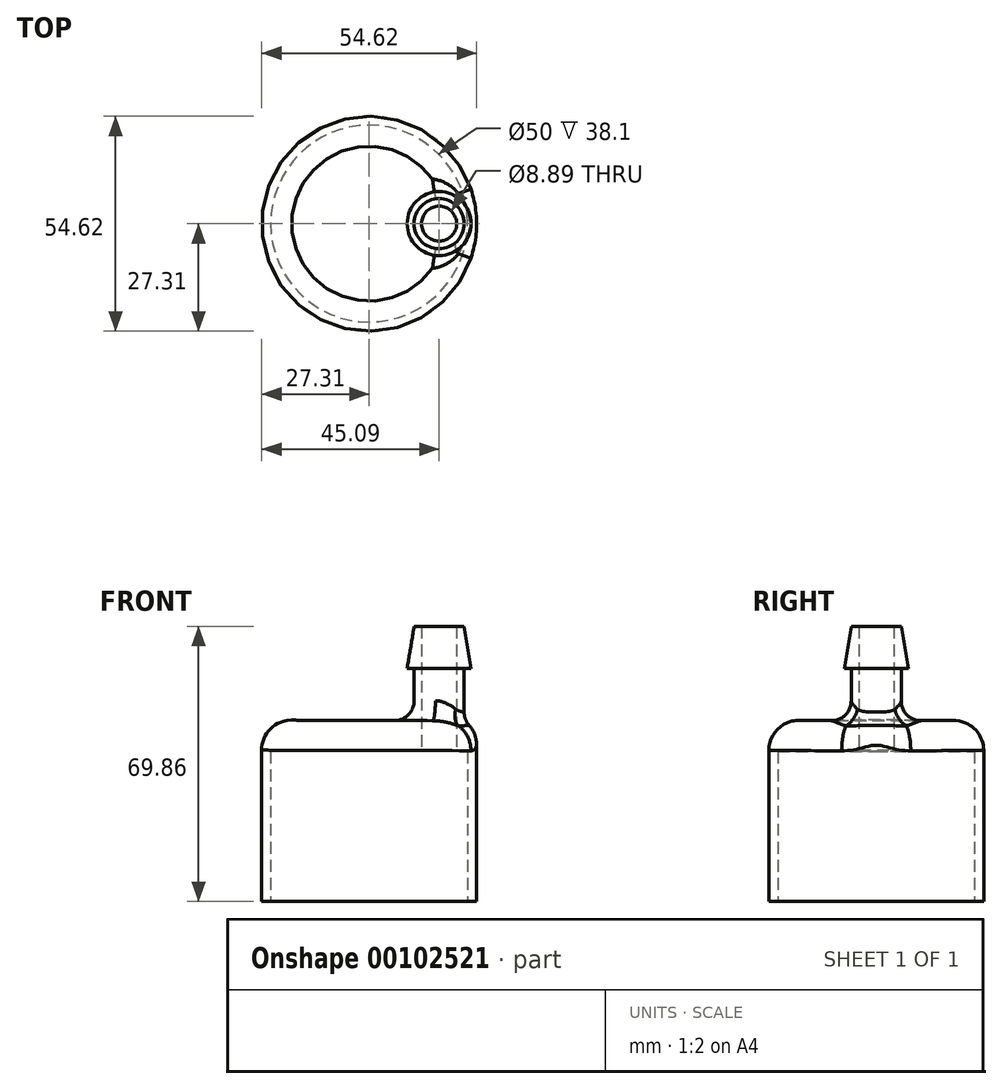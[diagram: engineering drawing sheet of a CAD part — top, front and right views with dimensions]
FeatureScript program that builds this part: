
annotation { "Feature Type Name" : "Feature", "Feature Type Description" : "" }
export const myFeature = defineFeature(function(context is Context, id is Id, definition is map)
    precondition{}
    {
        {
            var Q0;
            Q0=qCreatedBy(makeId("Top.planeOp"),FACE);
            var sketch = newSketch(context, id + "F0", { "sketchPlane" : qUnion([Q0])});
            skCircle(sketch, "E0", {"center": v(0, 0) * mm, "radius": 25 * mm});
            skCircle(sketch, "E1", {"center": v(0, 0) * mm, "radius": 27.3 * mm});
            skSolve(sketch);
        }
        {
            var Q0;
            Q0 = qSketchRegion(id + "F0", true);
            extrude(context, id + "F1", {"entities" : qUnion([Q0]), "depth" : 38.1 * mm});
        }
        {
            var Q0;
            Q0=qCreatedBy(makeId("Front.planeOp"),FACE);
            var sketch = newSketch(context, id + "F2", { "sketchPlane" : qUnion([Q0])});
            skLineSegment(sketch, "E2", {"start": v(24.13, 69.86) * mm, "end": v(22.22, 69.85) * mm});
            skLineSegment(sketch, "E3", {"start": v(25.9, 59.1) * mm, "end": v(24.13, 59.1) * mm});
            skLineSegment(sketch, "E4", {"start": v(22.23, 69.85) * mm, "end": v(22.23, 45.86) * mm});
            skLineSegment(sketch, "E5", {"start": v(22.23, 45.86) * mm, "end": v(24.13, 45.87) * mm});
            skLineSegment(sketch, "E6", {"start": v(17.78, 45.93) * mm, "end": v(17.78, 55.46) * mm});
            skLineSegment(sketch, "E7", {"start": v(24.13, 69.86) * mm, "end": v(25.9, 59.1) * mm});
            skLineSegment(sketch, "E8", {"start": v(24.13, 59.1) * mm, "end": v(24.13, 45.87) * mm});
            skSolve(sketch);
        }
        {
            var Q0;
            Q0 = qSketchRegion(id + "F2", true);
            var Q1;
            Q1=sQuery(id+"F2.wireOp",EDGE,"E6");
            revolve(context, id + "F3", {"entities" : qUnion([Q0]), "axis" : qUnion([Q1]), "revolveType" : RevolveType.FULL});
        }
        {
            var Q0;
            Q0=makeQuery(id+"F1.opExtrude","CAP_FACE",FACE,{"disambiguationData":[OSD([sQuery(id+"F0.wireOp",EDGE,"E0"),sQuery(id+"F0.wireOp",EDGE,"E1")])],"isStart":false});
            var sketch = newSketch(context, id + "F4", { "sketchPlane" : qUnion([Q0])});
            skCircle(sketch, "E9", {"center": v(0, 0) * mm, "radius": 27.3 * mm});
            skSolve(sketch);
        }
        {
            var Q0;
            Q0 = qSketchRegion(id + "F4", true);
            var Q1;
            Q1=makeQuery(id+"F3.opRevolve","SWEPT_FACE",FACE,{"disambiguationData":[OSD([sQuery(id+"F2.wireOp",EDGE,"E5")])]});
            extrude(context, id + "F5", {"entities" : qUnion([Q0]), "operationType" : NewBodyOperationType.ADD, "endBound" : BoundingType.UP_TO_SURFACE, "endBoundEntityFace" : qUnion([Q1]), "depth" : 25.4 * mm});
        }
        {
            var Q0;
            Q0=qCreatedBy(makeId("Top.planeOp"),FACE);
            var sketch = newSketch(context, id + "F6", { "sketchPlane" : qUnion([Q0])});
            skCircle(sketch, "E10", {"center": v(17.78, 0) * mm, "radius": 4.45 * mm});
            skSolve(sketch);
        }
        {
            var Q0;
            Q0 = qSketchRegion(id + "F6", true);
            extrude(context, id + "F7", {"entities" : qUnion([Q0]), "operationType" : NewBodyOperationType.REMOVE, "depth" : 76.2 * mm});
        }
        {
            var Q0;
            Q0=makeQuery(id+"F5.opExtrude","CAP_EDGE",EDGE,{"disambiguationData":[OSD([sQuery(id+"F4.wireOp",EDGE,"E9")])],"isStart":false});
            var Q1;
            Q1=makeQuery(id+"F1.opExtrude","CAP_EDGE",EDGE,{"disambiguationData":[OSD([sQuery(id+"F0.wireOp",EDGE,"E0")])],"isStart":false});
            fillet(context, id + "F8", {"entities" : qUnion([Q0, Q1]), "radius" : 7.62 * mm, "tangentPropagation" : true, "allowEdgeOverflow" : false});
        }
        {
            var Q0;
            Q0=makeQuery(id+"F3.opRevolve","SWEPT_EDGE",EDGE,{"disambiguationData":[OSD([sQuery(id+"F2.wireOp",EDGE,"E5"),sQuery(id+"F2.wireOp",EDGE,"E8")])]});
            fillet(context, id + "F9", {"entities" : qUnion([Q0]), "radius" : 5.08 * mm, "tangentPropagation" : true, "allowEdgeOverflow" : false});
        }
    });
